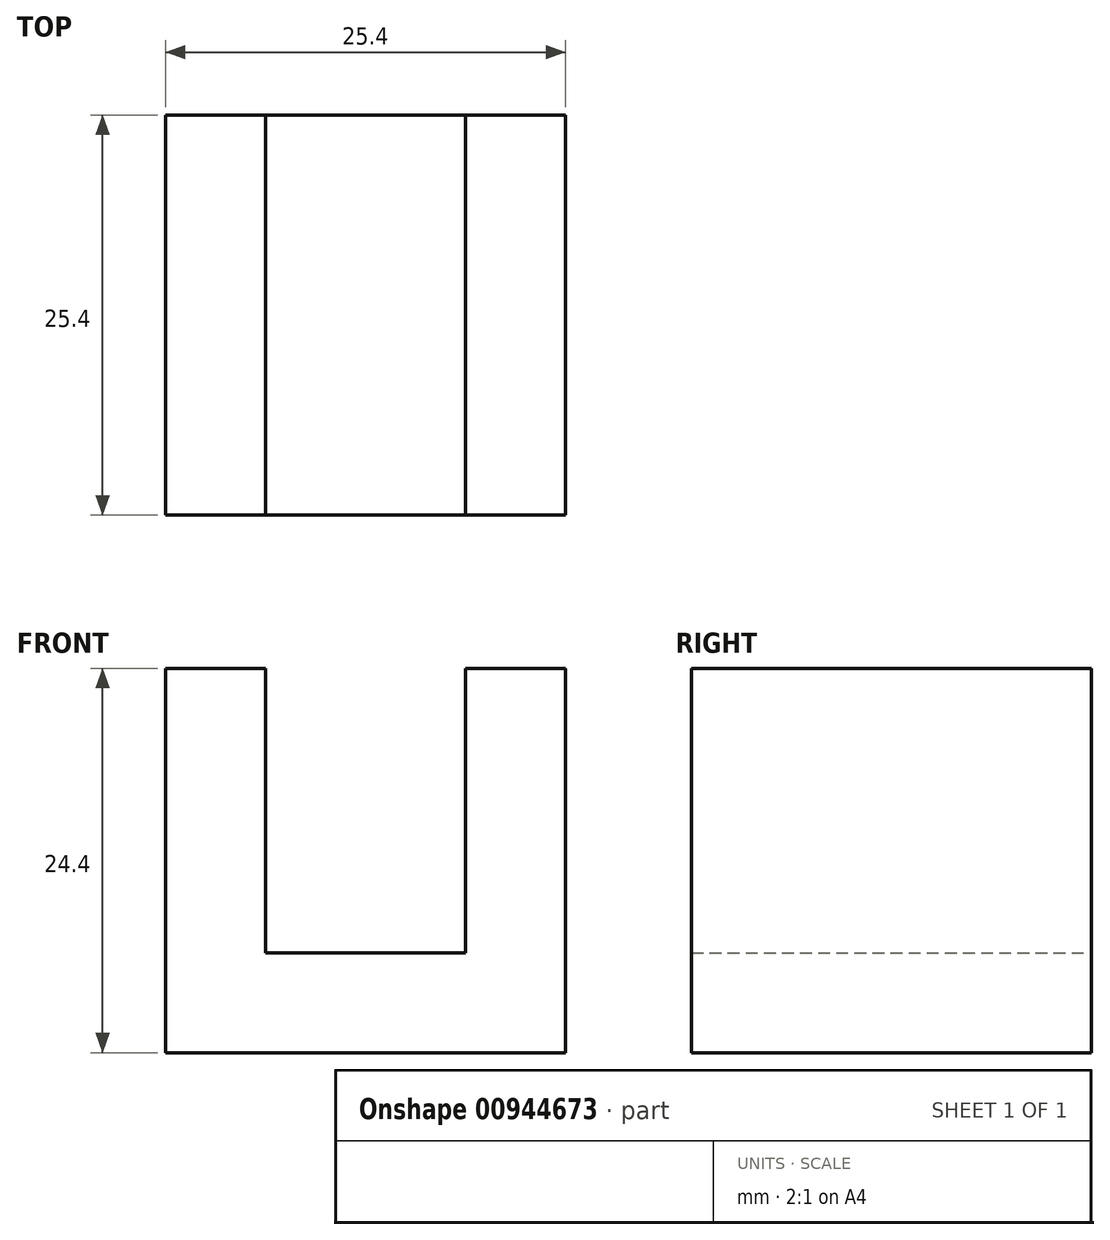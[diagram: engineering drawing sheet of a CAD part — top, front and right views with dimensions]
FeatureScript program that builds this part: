
annotation { "Feature Type Name" : "Feature", "Feature Type Description" : "" }
export const myFeature = defineFeature(function(context is Context, id is Id, definition is map)
    precondition{}
    {
        {
            var Q0;
            Q0=qCreatedBy(makeId("Front.planeOp"),FACE);
            var sketch = newSketch(context, id + "F0", { "sketchPlane" : qUnion([Q0])});
            skLineSegment(sketch, "E0.bottom", {"start": v(12.7, 12.2) * mm, "end": v(6.35, 12.2) * mm});
            skLineSegment(sketch, "E0.top", {"start": v(12.7, -12.2) * mm, "end": v(-12.7, -12.2) * mm});
            skLineSegment(sketch, "E0.left", {"start": v(12.7, 12.2) * mm, "end": v(12.7, -12.2) * mm});
            skLineSegment(sketch, "E0.right", {"start": v(-12.7, 12.2) * mm, "end": v(-12.7, -12.2) * mm});
            skPoint(sketch, "E0.middle", {"position": v(0, 0) * mm});
            skLineSegment(sketch, "E1.0", {"start": v(-6.35, 12.2) * mm, "end": v(-6.35, -5.85) * mm});
            skLineSegment(sketch, "E1.1", {"start": v(6.35, -5.85) * mm, "end": v(-6.35, -5.85) * mm});
            skLineSegment(sketch, "E1.2", {"start": v(6.35, 12.2) * mm, "end": v(6.35, -5.85) * mm});
            skLineSegment(sketch, "E2.trimOffspring", {"start": v(-6.35, 12.2) * mm, "end": v(-12.7, 12.2) * mm});
            skSolve(sketch);
        }
        {
            var Q0;
            Q0=makeQuery(id+"F0.imprint","IMPRINT",FACE,{"disambiguationData":[TD([[makeQuery(id+"F0.imprint","IMPRINT",EDGE,{"derivedFrom":sQuery(id+"F0.wireOp",EDGE,"E0.bottom")}),1.0]])]});
            extrude(context, id + "F1", {"entities" : qUnion([Q0]), "depth" : 25.4 * mm, "offsetDistance" : 25.4 * mm});
        }
    });
